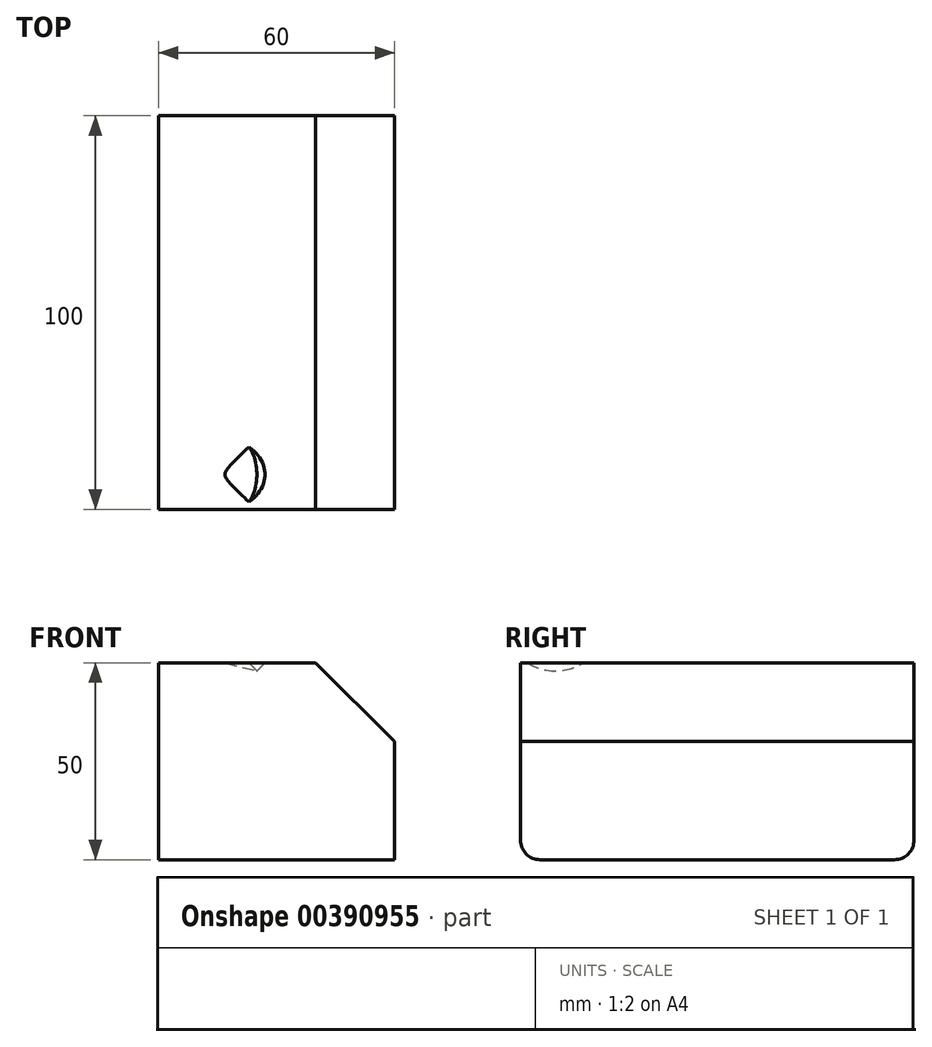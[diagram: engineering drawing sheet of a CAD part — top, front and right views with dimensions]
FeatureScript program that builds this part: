
annotation { "Feature Type Name" : "Feature", "Feature Type Description" : "" }
export const myFeature = defineFeature(function(context is Context, id is Id, definition is map)
    precondition{}
    {
        {
            var Q0;
            Q0=qCreatedBy(makeId("Top.planeOp"),FACE);
            var sketch = newSketch(context, id + "F0", { "sketchPlane" : qUnion([Q0])});
            skLineSegment(sketch, "E0.bottom", {"start": v(0, 0) * mm, "end": v(60, 0) * mm});
            skLineSegment(sketch, "E0.top", {"start": v(0, 100) * mm, "end": v(60, 100) * mm});
            skLineSegment(sketch, "E0.left", {"start": v(0, 0) * mm, "end": v(0, 100) * mm});
            skLineSegment(sketch, "E0.right", {"start": v(60, 0) * mm, "end": v(60, 100) * mm});
            skSolve(sketch);
        }
        {
            var Q0;
            Q0=makeQuery(id+"F0.imprint","IMPRINT",FACE,{"disambiguationData":[TD([[makeQuery(id+"F0.imprint","IMPRINT",EDGE,{"derivedFrom":sQuery(id+"F0.wireOp",EDGE,"E0.bottom")}),1.0]])]});
            extrude(context, id + "F1", {"entities" : qUnion([Q0]), "depth" : 50 * mm});
        }
        {
            var Q0;
            Q0=makeQuery(id+"F1.opExtrude","CAP_EDGE",EDGE,{"disambiguationData":[OSD([sQuery(id+"F0.wireOp",EDGE,"E0.right")])],"isStart":false});
            chamfer(context, id + "F2", {"entities" : qUnion([Q0]), "width" : 20 * mm, "tangentPropagation" : true});
        }
        {
            var Q0;
            Q0=makeQuery(id+"F2.opChamfer","BLEND_FACE",FACE,{"disambiguationData":[OSD([sQuery(id+"F0.wireOp",EDGE,"E0.right")])]});
            var sketch = newSketch(context, id + "F3", { "sketchPlane" : qUnion([Q0])});
            skPoint(sketch, "E1", {"position": v(8.88, 26.2) * mm});
            skPoint(sketch, "E2", {"position": v(8.88, 71.5) * mm});
            skSolve(sketch);
        }
        {
            var Q0;
            Q0=sQuery(id+"F3.wireOp",VERTEX,"E1");
            var Q1;
            Q1=sQuery(id+"F3.wireOp",VERTEX,"E2");
            var Q2;
            Q2=makeQuery(id+"F1.opExtrude","SWEPT_BODY",BODY,{"disambiguationData":[OSD([sQuery(id+"F0.wireOp",EDGE,"E0.bottom"),sQuery(id+"F0.wireOp",EDGE,"E0.top"),sQuery(id+"F0.wireOp",EDGE,"E0.left"),sQuery(id+"F0.wireOp",EDGE,"E0.right")])]});
            hole(context, id + "F4", {"style" : HoleStyle.SIMPLE, "endStyle" : HoleEndStyle.BLIND, "holeDiameter" : 20 * mm, "holeDepth" : 12 * mm, "isTappedThrough" : true, "tappedDepth" : 12 * mm, "tapClearance" : 3, "locations" : qUnion([Q0, Q1]), "scope" : qUnion([Q2])});
        }
        {
            var Q0;
            Q0=makeQuery(id+"F2.opChamfer","BLEND_FACE",FACE,{"disambiguationData":[OSD([sQuery(id+"F0.wireOp",EDGE,"E0.right")])]});
            var sketch = newSketch(context, id + "F5", { "sketchPlane" : qUnion([Q0])});
            skSolve(sketch);
        }
        {
            var Q0;
            Q0=makeQuery(id+"F1.opExtrude","CAP_EDGE",EDGE,{"disambiguationData":[OSD([sQuery(id+"F0.wireOp",EDGE,"E0.bottom")])],"isStart":true});
            fillet(context, id + "F6", {"entities" : qUnion([Q0]), "radius" : 5 * mm, "tangentPropagation" : true, "allowEdgeOverflow" : false});
        }
        {
            var Q0;
            Q0=makeQuery(id+"F1.opExtrude","CAP_EDGE",EDGE,{"disambiguationData":[OSD([sQuery(id+"F0.wireOp",EDGE,"E0.top")])],"isStart":true});
            fillet(context, id + "F7", {"entities" : qUnion([Q0]), "radius" : 5 * mm, "tangentPropagation" : true, "allowEdgeOverflow" : false});
        }
    });
